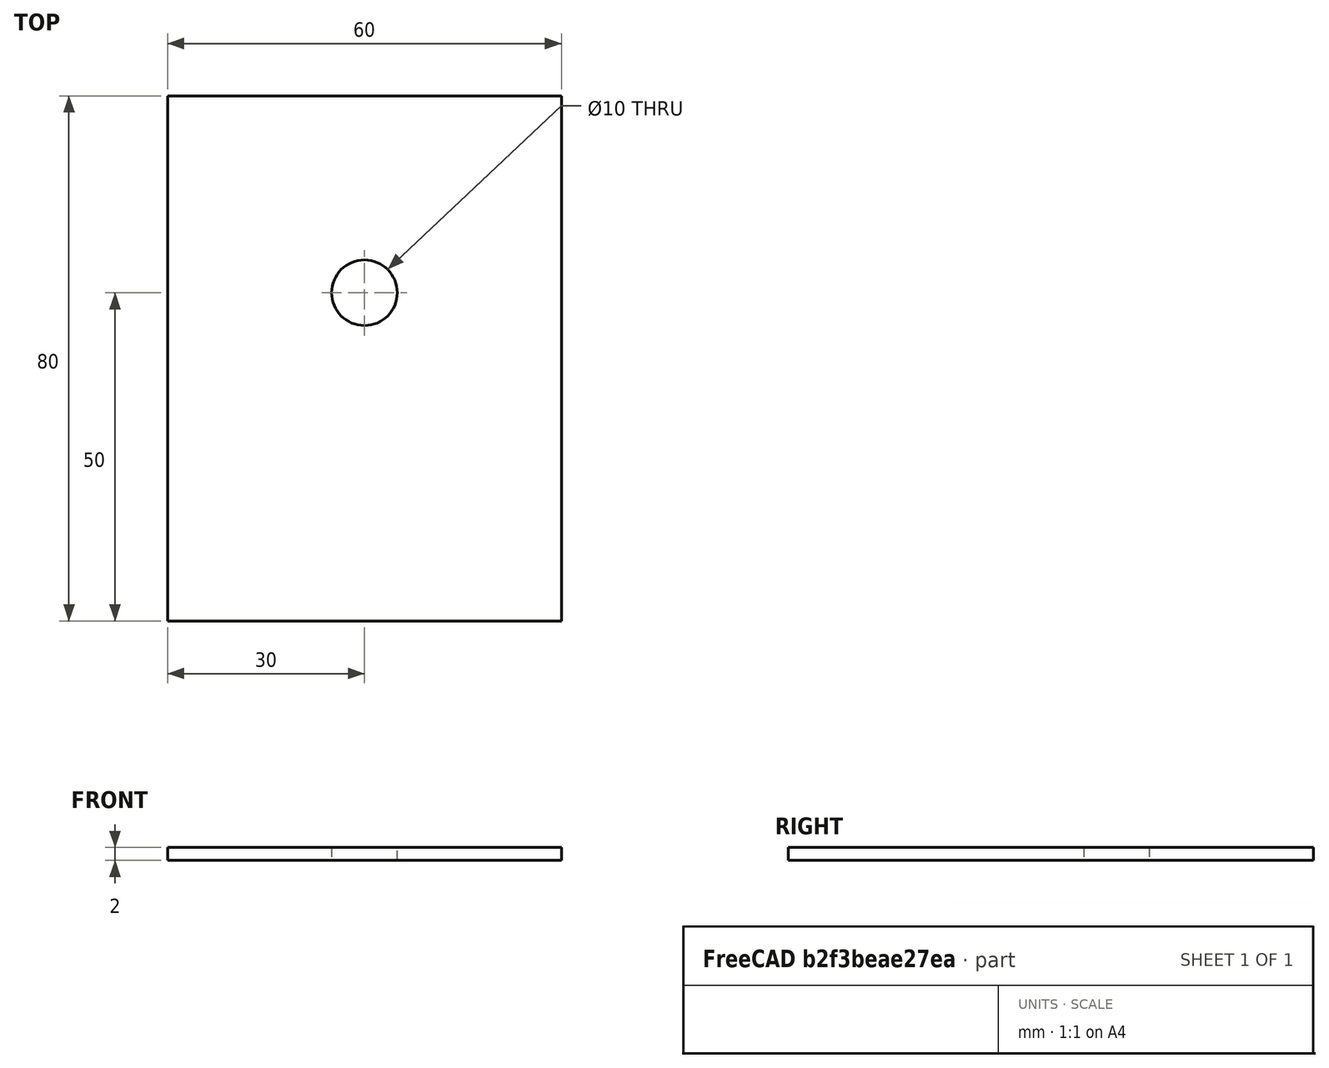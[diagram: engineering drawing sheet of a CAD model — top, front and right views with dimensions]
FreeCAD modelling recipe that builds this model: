
FCSTD DOCUMENT  (FreeCAD 0.15R4671 (Git))
Label: example 1
License: All rights reserved
LicenseURL: http://en.wikipedia.org/wiki/All_rights_reserved
objects: Sketcher::SketchObject×1, PartDesign::Pad×1
note: 3 computed .brp shape members not serialized (recipe doc carries the construction recipe); baked Part::Feature solids carry a one-line shape summary decoded from their .brp

FEATURE [Sketcher::SketchObject] Sketch  label="back plate sketch"
  sketch-geometry (5):
    g0: LineSegment StartX=-30 StartY=40 StartZ=0 EndX=30 EndY=40 EndZ=0
    g1: LineSegment StartX=30 StartY=40 StartZ=0 EndX=30 EndY=-40 EndZ=0
    g2: LineSegment StartX=30 StartY=-40 StartZ=0 EndX=-30 EndY=-40 EndZ=0
    g3: LineSegment StartX=-30 StartY=-40 StartZ=0 EndX=-30 EndY=40 EndZ=0
    g4: Circle CenterX=0 CenterY=10 CenterZ=0 NormalX=0 NormalY=0 NormalZ=1 Radius=5
  constraints (15):
    c: Coincident(g0,g1)
    c: Coincident(g1,g2)
    c: Coincident(g2,g3)
    c: Coincident(g3,g0)
    c: Horizontal(g0)
    c: Horizontal(g2)
    c: Vertical(g1)
    c: Vertical(g3)
    c: Symmetric(g2,g1,g-2)
    c: Symmetric(g0,g2,g-1)
    c: DistanceY(g0,g2) = -80
    c: DistanceX(g2,g1) = 60
    c: DistanceX(g-1,g4) = 0
    c: DistanceY(g-1,g4) = 10
    c: Radius(g4) = 5
FEATURE [PartDesign::Pad] Pad  label="back plate"
  Length = 2
  Length2 = 100
  Sketch = -> Sketch
  Type = 0
